# Revit family: ok-Celite_Universal_Assento para Bacia Sanitária_90981
name_source: partatom
category: Plumbing Fixtures
revit_build: Autodesk Revit MEP 2014 (Build: 20131024_2115(x64)
units: mm (PartAtom-declared; Revit-internal decimal feet)

## types (5) — shared parameters
Assembly Code = D2010400
Celite: Categoria = Assentos
Celite: Código = 90981
Celite: Fabricante = Celite
Celite: Linha = Universal
Celite: Link do Produto = http://www.celite.com.br
Celite: Norma = ABNT NBR 15097-1: 2011 - Requisitos e métodos de ensaio
Celite: Produto = Assentos
Celite: Tipo = Assentos para bacias
Celite: Versão = Autodesk Revit MEP 2014
Desenvolvido por = ofcdesk
Manufacturer = Celite
Model = 90981
Selo de Qualidade ofcdesk = Standard
URL = http://www.celite.com.br
zero-valued in all types: CWFU, Default Elevation, HWFU, WFU

## per-type parameters (varying)
| type | Celite: Cores Disponíveis | Celite: Descrição | Description |
| Pergamon - 90981 | Pergamon | Assento universal para bacia sanitária cor pergamon  (90981), linha Universal - Louças Celite | Assento universal para bacia sanitária cor pergamon  (90981), linha Universal - Louças Celite |
| Branco - 90981 | Branco | Assento universal para bacia sanitária cor branco (90981), linha Universal - Louças Celite | Assento universal para bacia sanitária cor branco (90981), linha Universal - Louças Celite |
| Cinza - 90981 | Cinza | Assento universal para bacia sanitária cor cinza (90981), linha Universal - Louças Celite | Assento universal para bacia sanitária cor cinza (90981), linha Universal - Louças Celite |
| Ocre - 90981 | Ocre | Assento universal para bacia sanitária cor ocre (90981), linha Universal - Louças Celite | Assento universal para bacia sanitária cor ocre (90981), linha Universal - Louças Celite |
| Cinza prata - 90981 | Cinza prata | Assento universal para bacia sanitária cor cinza prata (90981), linha Universal - Louças Celite | Assento universal para bacia sanitária cor cinza prata (90981), linha Universal - Louças Celite |

## geometry (parser evidence)
native form markers: Blend x4, Sweep x2
no freeform markers — native parametric forms only
